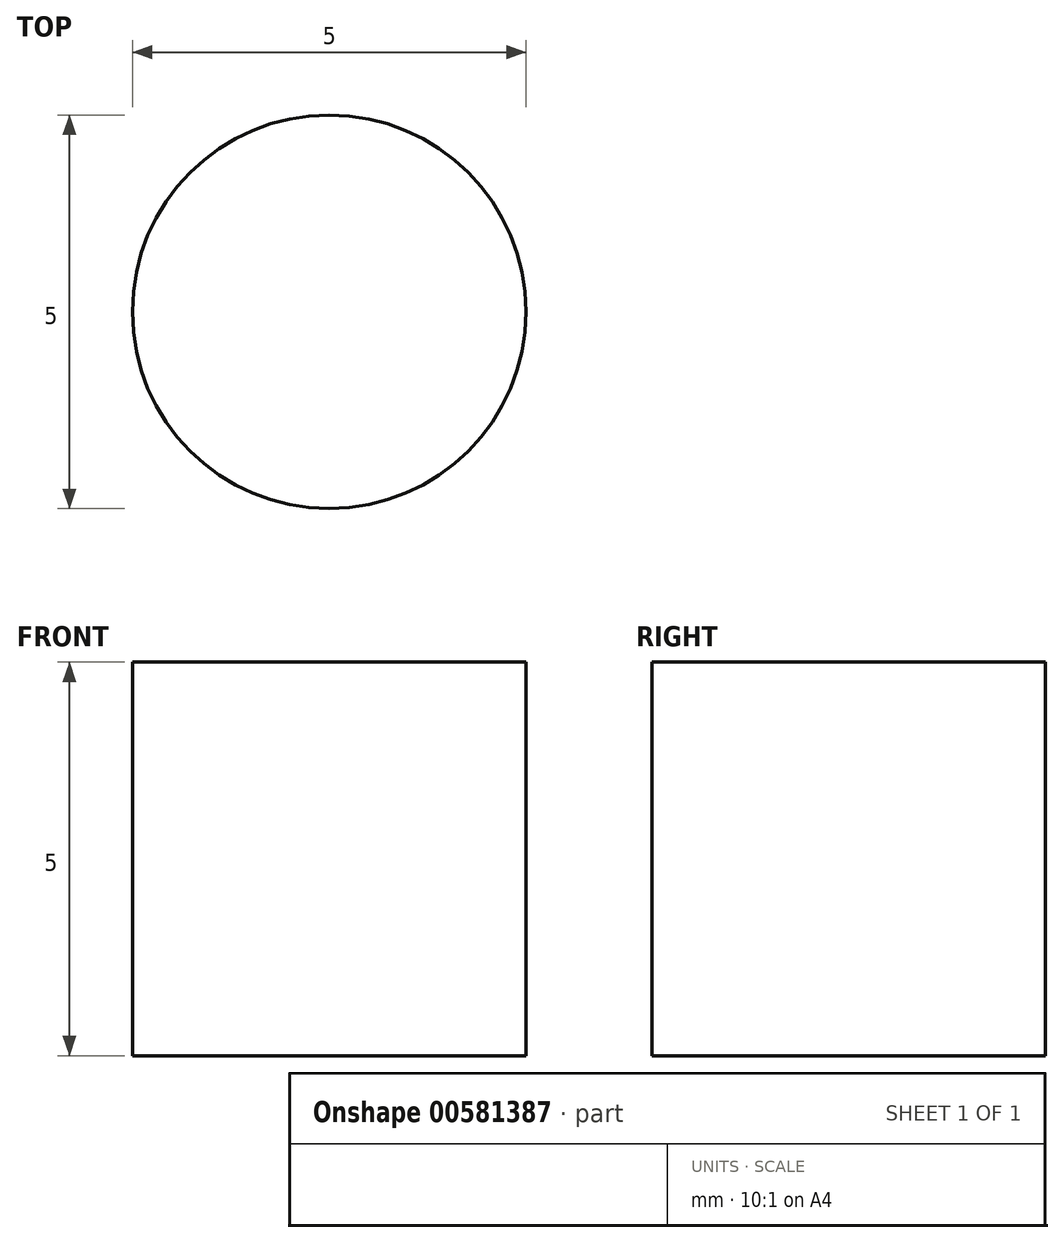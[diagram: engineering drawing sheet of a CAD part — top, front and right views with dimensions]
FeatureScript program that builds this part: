
annotation { "Feature Type Name" : "Feature", "Feature Type Description" : "" }
export const myFeature = defineFeature(function(context is Context, id is Id, definition is map)
    precondition{}
    {
        {
            var Q0;
            Q0=qCreatedBy(makeId("Top.planeOp"),FACE);
            var sketch = newSketch(context, id + "F0", { "sketchPlane" : qUnion([Q0])});
            skCircle(sketch, "E0", {"center": v(0, 0) * mm, "radius": 2.5 * mm});
            skSolve(sketch);
        }
        {
            var Q0;
            Q0=makeQuery(id+"F0.imprint","IMPRINT",FACE,{"disambiguationData":[TD([[makeQuery(id+"F0.imprint","IMPRINT",EDGE,{"derivedFrom":sQuery(id+"F0.wireOp",EDGE,"E0")}),1.0]])]});
            extrude(context, id + "F1", {"entities" : qUnion([Q0]), "depth" : 5 * mm, "offsetDistance" : 25 * mm});
        }
    });
